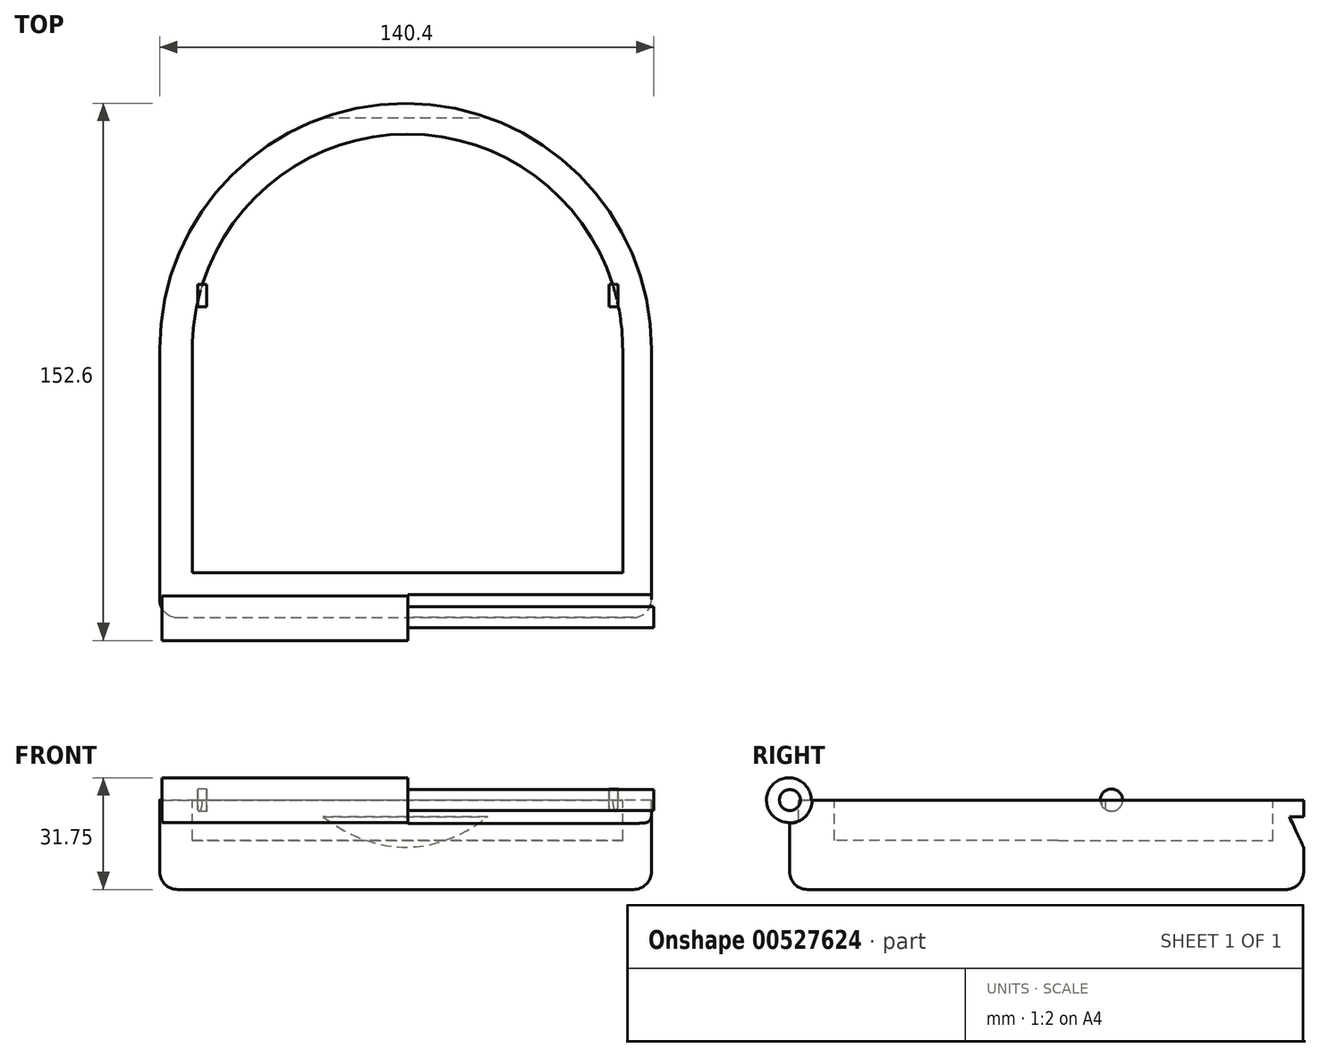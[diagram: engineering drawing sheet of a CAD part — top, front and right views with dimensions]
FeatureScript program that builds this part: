
annotation { "Feature Type Name" : "Feature", "Feature Type Description" : "" }
export const myFeature = defineFeature(function(context is Context, id is Id, definition is map)
    precondition{}
    {
        {
            var Q0;
            Q0=qCreatedBy(makeId("Top.planeOp"),FACE);
            var sketch = newSketch(context, id + "F0", { "sketchPlane" : qUnion([Q0])});
            skArc(sketch, "E0", {"start": v(69.15, 0) * mm, "mid": v(-0.7, 69.85) * mm, "end": v(-70.55, 0) * mm});
            skLineSegment(sketch, "E1", {"start": v(-70.55, 0) * mm, "end": v(-70.55, -76.2) * mm});
            skLineSegment(sketch, "E2", {"start": v(-70.55, -76.2) * mm, "end": v(69.15, -76.2) * mm});
            skLineSegment(sketch, "E3", {"start": v(69.15, -76.2) * mm, "end": v(69.15, 0) * mm});
            skSolve(sketch);
        }
        {
            var Q0;
            Q0=qCreatedBy(makeId("Right.planeOp"),FACE);
            var sketch = newSketch(context, id + "F1", { "sketchPlane" : qUnion([Q0])});
            skCircle(sketch, "E4", {"center": v(-76.4, 0) * mm, "radius": 6.35 * mm});
            skSolve(sketch);
        }
        {
            var Q0;
            Q0=qCreatedBy(makeId("Right.planeOp"),FACE);
            var sketch = newSketch(context, id + "F2", { "sketchPlane" : qUnion([Q0])});
            skCircle(sketch, "E5", {"center": v(-76.1, 0) * mm, "radius": 2.98 * mm});
            skSolve(sketch);
        }
        {
            var Q0;
            Q0=qCreatedBy(makeId("Right.planeOp"),FACE);
            var sketch = newSketch(context, id + "F3", { "sketchPlane" : qUnion([Q0])});
            skCircle(sketch, "E6", {"center": v(-76.37, 0) * mm, "radius": 6.6 * mm});
            skSolve(sketch);
        }
        {
            var Q0;
            Q0 = qSketchRegion(id + "F0", true);
            extrude(context, id + "F4", {"entities" : qUnion([Q0]), "oppositeDirection" : true, "depth" : 25.4 * mm, "offsetDistance" : 25.4 * mm});
        }
        {
            var Q0;
            Q0 = qSketchRegion(id + "F1", true);
            extrude(context, id + "F5", {"entities" : qUnion([Q0]), "operationType" : NewBodyOperationType.ADD, "oppositeDirection" : true, "depth" : 69.85 * mm, "offsetDistance" : 25.4 * mm});
        }
        {
            var Q0;
            Q0 = qSketchRegion(id + "F3", true);
            extrude(context, id + "F6", {"entities" : qUnion([Q0]), "operationType" : NewBodyOperationType.REMOVE, "oppositeDirection" : true, "depth" : -69.85 * mm, "offsetDistance" : 25.4 * mm});
        }
        {
            var Q0;
            Q0=makeQuery(id+"F4.opExtrude","CAP_EDGE",EDGE,{"disambiguationData":[OSD([sQuery(id+"F0.wireOp",EDGE,"E2")])],"isStart":false});
            var Q1;
            Q1=makeQuery(id+"F4.opExtrude","CAP_EDGE",EDGE,{"disambiguationData":[OSD([sQuery(id+"F0.wireOp",EDGE,"E1")])],"isStart":false});
            var Q2;
            Q2=makeQuery(id+"F4.opExtrude","SWEPT_EDGE",EDGE,{"disambiguationData":[OSD([sQuery(id+"F0.wireOp",EDGE,"E1"),sQuery(id+"F0.wireOp",EDGE,"E2")])]});
            var Q3;
            Q3=makeQuery(id+"F4.opExtrude","SWEPT_EDGE",EDGE,{"disambiguationData":[OSD([sQuery(id+"F0.wireOp",EDGE,"E2"),sQuery(id+"F0.wireOp",EDGE,"E3")])]});
            fillet(context, id + "F7", {"entities" : qUnion([Q0, Q1, Q2, Q3]), "radius" : 5.08 * mm, "tangentPropagation" : true, "allowEdgeOverflow" : false});
        }
        {
            var Q0;
            Q0 = qSketchRegion(id + "F2", true);
            extrude(context, id + "F8", {"entities" : qUnion([Q0]), "operationType" : NewBodyOperationType.ADD, "depth" : 69.85 * mm, "offsetDistance" : 25.4 * mm});
        }
        {
            var Q0;
            Q0=qCreatedBy(makeId("Top.planeOp"),FACE);
            var sketch = newSketch(context, id + "F9", { "sketchPlane" : qUnion([Q0])});
            skArc(sketch, "E7", {"start": v(61, 0) * mm, "mid": v(-0.12, 61.11) * mm, "end": v(-61.23, 0) * mm});
            skLineSegment(sketch, "E8", {"start": v(-61.23, 0) * mm, "end": v(-61.23, -63.5) * mm});
            skLineSegment(sketch, "E9", {"start": v(61, 0) * mm, "end": v(61, -63.5) * mm});
            skLineSegment(sketch, "E10", {"start": v(-61.23, -63.5) * mm, "end": v(61, -63.5) * mm});
            skSolve(sketch);
        }
        {
            var Q0;
            Q0 = qSketchRegion(id + "F9", true);
            extrude(context, id + "F10", {"entities" : qUnion([Q0]), "operationType" : NewBodyOperationType.REMOVE, "oppositeDirection" : true, "depth" : 11.43 * mm, "offsetDistance" : 25.4 * mm});
        }
        {
            var Q0;
            Q0=qCreatedBy(makeId("Right.planeOp"),FACE);
            var sketch = newSketch(context, id + "F11", { "sketchPlane" : qUnion([Q0])});
            skLineSegment(sketch, "E11", {"start": v(69.86, 0) * mm, "end": v(69.86, -4.73) * mm});
            skLineSegment(sketch, "E12", {"start": v(69.86, -4.73) * mm, "end": v(65.8, -4.73) * mm});
            skLineSegment(sketch, "E13", {"start": v(65.8, -4.73) * mm, "end": v(71.38, -16.7) * mm});
            skLineSegment(sketch, "E14", {"start": v(71.38, -16.7) * mm, "end": v(69.86, 0) * mm});
            skSolve(sketch);
        }
        {
            var Q0;
            Q0 = qSketchRegion(id + "F11", true);
            extrude(context, id + "F12", {"entities" : qUnion([Q0]), "operationType" : NewBodyOperationType.REMOVE, "oppositeDirection" : true, "depth" : 25.4 * mm, "offsetDistance" : 25.4 * mm, "hasSecondDirection" : true, "secondDirectionOppositeDirection" : false, "secondDirectionDepth" : 25.4 * mm});
        }
        {
            var Q0;
            Q0=qCreatedBy(makeId("Right.planeOp"),FACE);
            var sketch = newSketch(context, id + "F13", { "sketchPlane" : qUnion([Q0])});
            skCircle(sketch, "E15", {"center": v(15.24, 0) * mm, "radius": 3.17 * mm});
            skSolve(sketch);
        }
        {
            var Q0;
            Q0 = qSketchRegion(id + "F13", true);
            extrude(context, id + "F14", {"entities" : qUnion([Q0]), "operationType" : NewBodyOperationType.ADD, "depth" : 59.69 * mm, "offsetDistance" : 25.4 * mm, "hasSecondDirection" : true, "secondDirectionOppositeDirection" : true, "secondDirectionDepth" : 59.69 * mm});
        }
        {
            var Q0;
            Q0=qCreatedBy(makeId("Right.planeOp"),FACE);
            var sketch = newSketch(context, id + "F15", { "sketchPlane" : qUnion([Q0])});
            skCircle(sketch, "E16", {"center": v(15.24, 0) * mm, "radius": 3.19 * mm});
            skSolve(sketch);
        }
        {
            var Q0;
            Q0 = qSketchRegion(id + "F15", true);
            extrude(context, id + "F16", {"entities" : qUnion([Q0]), "operationType" : NewBodyOperationType.REMOVE, "oppositeDirection" : true, "depth" : 57.15 * mm, "offsetDistance" : 25.4 * mm, "hasSecondDirection" : true, "secondDirectionOppositeDirection" : false, "secondDirectionDepth" : 57.15 * mm});
        }
    });
